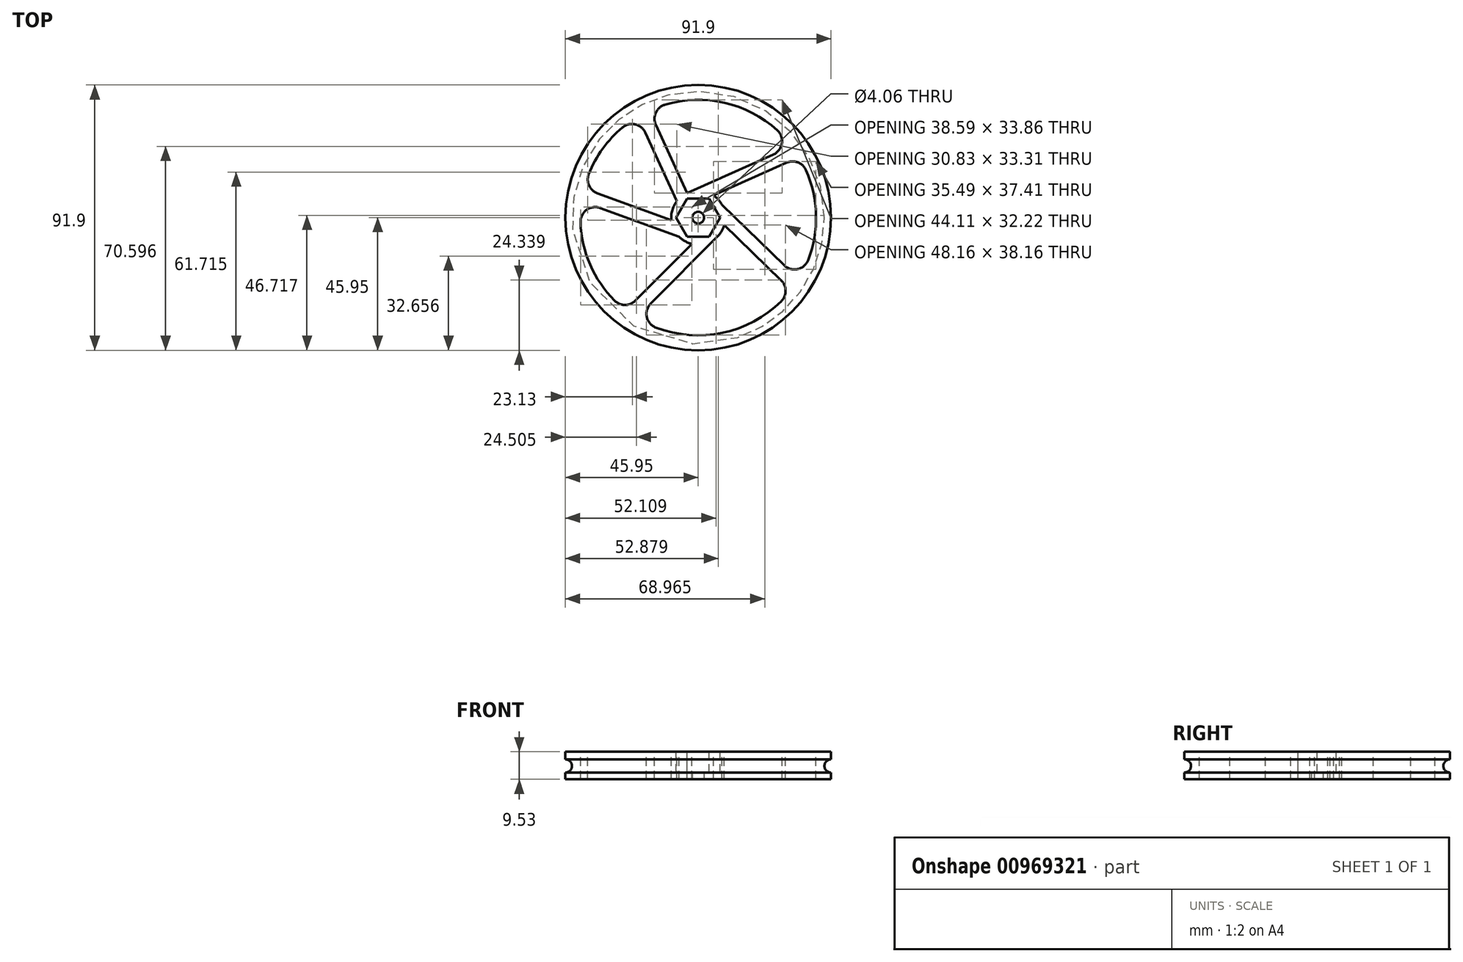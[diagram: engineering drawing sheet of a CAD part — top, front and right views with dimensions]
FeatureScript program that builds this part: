
annotation { "Feature Type Name" : "Feature", "Feature Type Description" : "" }
export const myFeature = defineFeature(function(context is Context, id is Id, definition is map)
    precondition{}
    {
        {
            var Q0;
            Q0=qCreatedBy(makeId("Top.planeOp"),FACE);
            var sketch = newSketch(context, id + "F0", { "sketchPlane" : qUnion([Q0])});
            skCircle(sketch, "E0", {"center": v(0, 0) * mm, "radius": 44.45 * mm});
            skCircle(sketch, "E1", {"center": v(0, 0) * mm, "radius": 40.77 * mm});
            skCircle(sketch, "E2.cCircle", {"center": v(0, 0) * mm, "radius": 6.6 * mm, "construction": true});
            skLineSegment(sketch, "E2.0", {"start": v(3.81, 6.6) * mm, "end": v(7.63, 0) * mm});
            skLineSegment(sketch, "E2.1", {"start": v(7.63, 0) * mm, "end": v(3.81, -6.6) * mm});
            skLineSegment(sketch, "E2.2", {"start": v(3.81, -6.6) * mm, "end": v(-3.81, -6.6) * mm});
            skLineSegment(sketch, "E2.3", {"start": v(-3.81, -6.6) * mm, "end": v(-7.63, 0) * mm});
            skLineSegment(sketch, "E2.4", {"start": v(-7.63, 0) * mm, "end": v(-3.81, 6.6) * mm});
            skLineSegment(sketch, "E2.5", {"start": v(-3.81, 6.6) * mm, "end": v(3.81, 6.6) * mm});
            skPoint(sketch, "E2.0.midPoint", {"position": v(5.72, 3.3) * mm});
            skPoint(sketch, "E3.end.orphan", {"position": v(39.33, -10.76) * mm});
            skPoint(sketch, "E4.startSnap0", {"position": v(5.72, -3.3) * mm});
            skPoint(sketch, "E5.end.orphan", {"position": v(23.47, 33.35) * mm});
            skPoint(sketch, "E6.end.orphan", {"position": v(29.65, 27.98) * mm});
            skPoint(sketch, "E7.end.orphan", {"position": v(-40.7, -2.3) * mm});
            skPoint(sketch, "E8.orphan", {"position": v(-29.65, 27.98) * mm});
            skPoint(sketch, "E9.orphan", {"position": v(-23.47, 33.35) * mm});
            skCircle(sketch, "E10", {"center": v(0, 0) * mm, "radius": 9.35 * mm});
            skLineSegment(sketch, "E11", {"start": v(6.62, -6.6) * mm, "end": v(-21.41, -34.7) * mm});
            skLineSegment(sketch, "E12", {"start": v(-3.81, 8.54) * mm, "end": v(32.42, 24.72) * mm});
            skLineSegment(sketch, "E13", {"start": v(-2.15, -9.1) * mm, "end": v(-25.12, -32.12) * mm});
            skLineSegment(sketch, "E14", {"start": v(5.27, 7.72) * mm, "end": v(34.96, 20.98) * mm});
            skPoint(sketch, "E15.end.orphan", {"position": v(40.24, -6.6) * mm});
            skLineSegment(sketch, "E16", {"start": v(8.25, 4.4) * mm, "end": v(34.74, -21.35) * mm});
            skLineSegment(sketch, "E17", {"start": v(9, -2.53) * mm, "end": v(32.17, -25.05) * mm});
            skLineSegment(sketch, "E18", {"start": v(-6.62, -6.6) * mm, "end": v(-40.37, 5.7) * mm});
            skLineSegment(sketch, "E19", {"start": v(-7.63, 0) * mm, "end": v(-9.33, 0.62) * mm});
            skLineSegment(sketch, "E20", {"start": v(-7.4, 5.7) * mm, "end": v(-20.88, 35.02) * mm});
            skLineSegment(sketch, "E21", {"start": v(-3.81, 8.54) * mm, "end": v(-16.94, 37.09) * mm});
            skLineSegment(sketch, "E22", {"start": v(-9.3, -0.9) * mm, "end": v(-39.5, 10.12) * mm});
            skSolve(sketch);
        }
        {
            var Q0;
            Q0=qCreatedBy(makeId("Front.planeOp"),FACE);
            var sketch = newSketch(context, id + "F1", { "sketchPlane" : qUnion([Q0])});
            skLineSegment(sketch, "E23", {"start": v(45.95, 0) * mm, "end": v(45.95, -2.62) * mm});
            skLineSegment(sketch, "E24", {"start": v(0, -9.53) * mm, "end": v(45.95, -9.53) * mm});
            skLineSegment(sketch, "E25", {"start": v(0, 0) * mm, "end": v(45.95, 0) * mm});
            skArc(sketch, "E26", {"start": v(45.95, -2.62) * mm, "mid": v(43.67, -4.9) * mm, "end": v(45.95, -7.2) * mm});
            skLineSegment(sketch, "E27", {"start": v(0, 0) * mm, "end": v(0, -9.53) * mm});
            skPoint(sketch, "E28.end.orphan", {"position": v(-44.72, -9.53) * mm});
            skPoint(sketch, "E28.start.orphan", {"position": v(-44.72, 0) * mm});
            skLineSegment(sketch, "E29.trimOffspring", {"start": v(45.95, -7.2) * mm, "end": v(45.95, -9.53) * mm});
            skSolve(sketch);
        }
        {
            var Q0;
            Q0=makeQuery(id+"F1.imprint","IMPRINT",FACE,{"disambiguationData":[TD([[makeQuery(id+"F1.imprint","IMPRINT",EDGE,{"derivedFrom":sQuery(id+"F1.wireOp",EDGE,"E23")}),-1.0]])]});
            var Q1;
            Q1=sQuery(id+"F1.wireOp",EDGE,"E27");
            revolve(context, id + "F2", {"surfaceOperationType" : NewSurfaceOperationType.NEW, "entities" : qUnion([Q0]), "axis" : qUnion([Q1]), "revolveType" : RevolveType.FULL});
        }
        {
            var Q0;
            Q0=makeQuery(id+"F2.opRevolve","SWEPT_FACE",FACE,{"disambiguationData":[OSD([sQuery(id+"F1.wireOp",EDGE,"E24")])]});
            var sketch = newSketch(context, id + "F3", { "sketchPlane" : qUnion([Q0])});
            skCircle(sketch, "E30", {"center": v(0, 0) * mm, "radius": 2.03 * mm});
            skSolve(sketch);
        }
        {
            var Q0;
            Q0=makeQuery(id+"F3.imprint","IMPRINT",FACE,{"disambiguationData":[TD([[makeQuery(id+"F3.imprint","IMPRINT",EDGE,{"derivedFrom":sQuery(id+"F3.wireOp",EDGE,"E30")}),1.0]])]});
            extrude(context, id + "F4", {"entities" : qUnion([Q0]), "operationType" : NewBodyOperationType.REMOVE, "endBound" : BoundingType.THROUGH_ALL, "oppositeDirection" : true, "depth" : 25.4 * mm, "offsetDistance" : 25.4 * mm});
        }
        {
            var Q0;
            {var subQ0=sQuery(id+"F0.wireOp",EDGE,"E12");Q0=makeQuery(id+"F0.imprint","IMPRINT",FACE,{"disambiguationData":[TD([[makeQuery(id+"F0.imprint","IMPRINT",EDGE,{"derivedFrom":subQ0}),1.0]])]});}
            var Q1;
            {var subQ3=sQuery(id+"F0.wireOp",EDGE,"E20");Q1=makeQuery(id+"F0.imprint","IMPRINT",FACE,{"disambiguationData":[TD([[makeQuery(id+"F0.imprint","IMPRINT",EDGE,{"derivedFrom":subQ3}),1.0]])]});}
            var Q2;
            {var subQ0=sQuery(id+"F0.wireOp",EDGE,"E13");Q2=makeQuery(id+"F0.imprint","IMPRINT",FACE,{"disambiguationData":[TD([[makeQuery(id+"F0.imprint","IMPRINT",EDGE,{"derivedFrom":subQ0}),-1.0]])]});}
            var Q3;
            {var subQ0=sQuery(id+"F0.wireOp",EDGE,"E11");Q3=makeQuery(id+"F0.imprint","IMPRINT",FACE,{"disambiguationData":[TD([[makeQuery(id+"F0.imprint","IMPRINT",EDGE,{"derivedFrom":subQ0}),1.0]])]});}
            var Q4;
            {var subQ0=sQuery(id+"F0.wireOp",EDGE,"E14");Q4=makeQuery(id+"F0.imprint","IMPRINT",FACE,{"disambiguationData":[TD([[makeQuery(id+"F0.imprint","IMPRINT",EDGE,{"derivedFrom":subQ0}),-1.0]])]});}
            extrude(context, id + "F5", {"entities" : qUnion([Q0, Q1, Q2, Q3, Q4]), "operationType" : NewBodyOperationType.REMOVE, "endBound" : BoundingType.THROUGH_ALL, "oppositeDirection" : true, "depth" : 25.4 * mm, "offsetDistance" : 25.4 * mm});
        }
        {
            var Q0;
            Q0=makeQuery(id+"F0.imprint","IMPRINT",FACE,{"disambiguationData":[TD([[makeQuery(id+"F0.imprint","IMPRINT",EDGE,{"derivedFrom":sQuery(id+"F0.wireOp",EDGE,"E2.0")}),-1.0]])]});
            extrude(context, id + "F6", {"entities" : qUnion([Q0]), "operationType" : NewBodyOperationType.REMOVE, "oppositeDirection" : true, "depth" : 7.26 * mm, "offsetDistance" : 25.4 * mm});
        }
        {
            var Q0;
            Q0=makeQuery(id+"F5.boolean.opBoolean","COPY",EDGE,{"derivedFrom":makeQuery(id+"F5.opExtrude","SWEPT_EDGE",EDGE,{"disambiguationData":[OSD([sQuery(id+"F0.wireOp",EDGE,"E1"),sQuery(id+"F0.wireOp",EDGE,"E14")])]})});
            var Q1;
            Q1=makeQuery(id+"F5.boolean.opBoolean","COPY",EDGE,{"derivedFrom":makeQuery(id+"F5.opExtrude","SWEPT_EDGE",EDGE,{"disambiguationData":[OSD([sQuery(id+"F0.wireOp",EDGE,"E1"),sQuery(id+"F0.wireOp",EDGE,"E12")])]})});
            var Q2;
            Q2=makeQuery(id+"F5.boolean.opBoolean","COPY",EDGE,{"derivedFrom":makeQuery(id+"F5.opExtrude","SWEPT_EDGE",EDGE,{"disambiguationData":[OSD([sQuery(id+"F0.wireOp",EDGE,"E1"),sQuery(id+"F0.wireOp",EDGE,"E21")])]})});
            var Q3;
            Q3=makeQuery(id+"F5.boolean.opBoolean","COPY",EDGE,{"derivedFrom":makeQuery(id+"F5.opExtrude","SWEPT_EDGE",EDGE,{"disambiguationData":[OSD([sQuery(id+"F0.wireOp",EDGE,"E1"),sQuery(id+"F0.wireOp",EDGE,"E20")])]})});
            var Q4;
            Q4=makeQuery(id+"F5.boolean.opBoolean","COPY",EDGE,{"derivedFrom":makeQuery(id+"F5.opExtrude","SWEPT_EDGE",EDGE,{"disambiguationData":[OSD([sQuery(id+"F0.wireOp",EDGE,"E1"),sQuery(id+"F0.wireOp",EDGE,"E22")])]})});
            var Q5;
            Q5=makeQuery(id+"F5.boolean.opBoolean","COPY",EDGE,{"derivedFrom":makeQuery(id+"F5.opExtrude","SWEPT_EDGE",EDGE,{"disambiguationData":[OSD([sQuery(id+"F0.wireOp",EDGE,"E1"),sQuery(id+"F0.wireOp",EDGE,"E18")])]})});
            var Q6;
            Q6=makeQuery(id+"F5.boolean.opBoolean","COPY",EDGE,{"derivedFrom":makeQuery(id+"F5.opExtrude","SWEPT_EDGE",EDGE,{"disambiguationData":[OSD([sQuery(id+"F0.wireOp",EDGE,"E1"),sQuery(id+"F0.wireOp",EDGE,"E11")])]})});
            var Q7;
            Q7=makeQuery(id+"F5.boolean.opBoolean","COPY",EDGE,{"derivedFrom":makeQuery(id+"F5.opExtrude","SWEPT_EDGE",EDGE,{"disambiguationData":[OSD([sQuery(id+"F0.wireOp",EDGE,"E1"),sQuery(id+"F0.wireOp",EDGE,"E13")])]})});
            var Q8;
            Q8=makeQuery(id+"F5.boolean.opBoolean","COPY",EDGE,{"derivedFrom":makeQuery(id+"F5.opExtrude","SWEPT_EDGE",EDGE,{"disambiguationData":[OSD([sQuery(id+"F0.wireOp",EDGE,"E1"),sQuery(id+"F0.wireOp",EDGE,"E17")])]})});
            var Q9;
            Q9=makeQuery(id+"F5.boolean.opBoolean","COPY",EDGE,{"derivedFrom":makeQuery(id+"F5.opExtrude","SWEPT_EDGE",EDGE,{"disambiguationData":[OSD([sQuery(id+"F0.wireOp",EDGE,"E1"),sQuery(id+"F0.wireOp",EDGE,"E16")])]})});
            fillet(context, id + "F7", {"entities" : qUnion([Q0, Q1, Q2, Q3, Q4, Q5, Q6, Q7, Q8, Q9]), "radius" : 5.08 * mm, "tangentPropagation" : true, "allowEdgeOverflow" : false});
        }
    });
